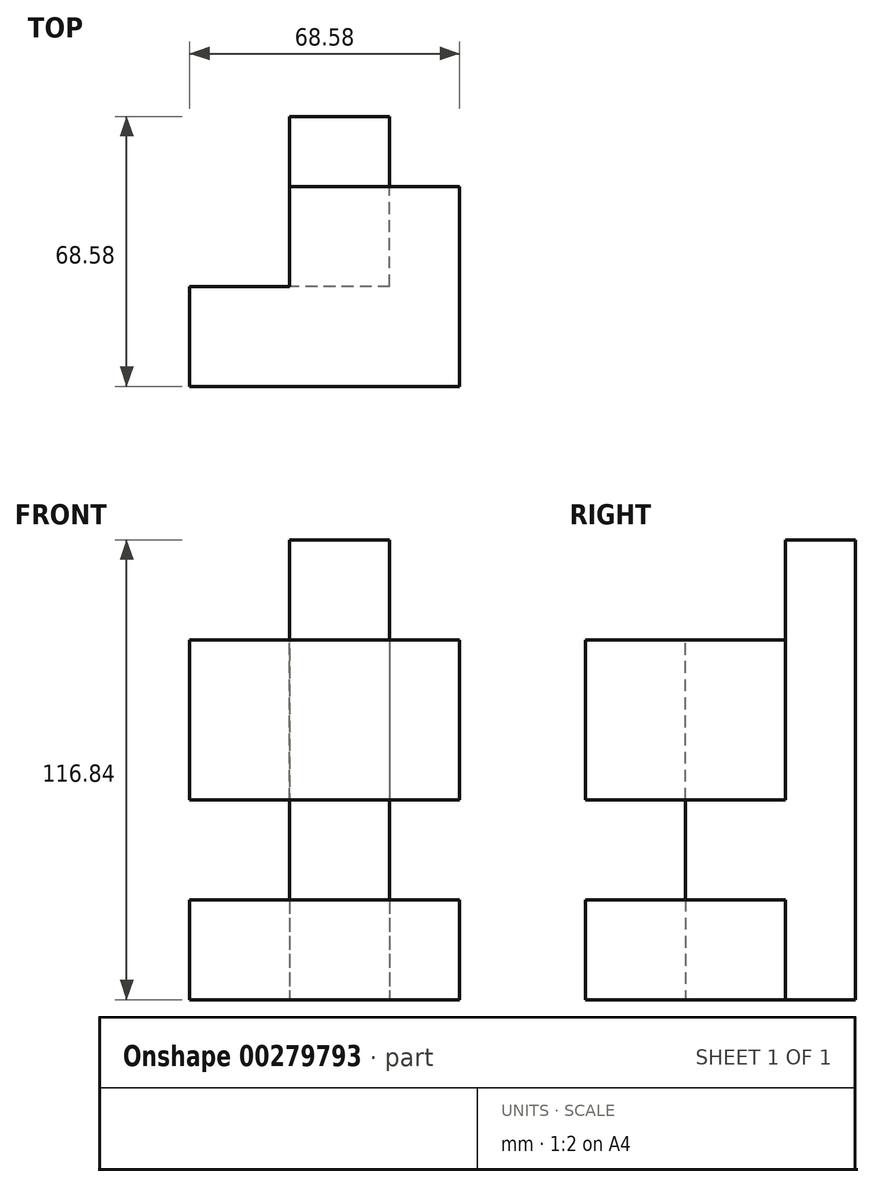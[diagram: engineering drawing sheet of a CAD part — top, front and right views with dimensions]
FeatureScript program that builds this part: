
annotation { "Feature Type Name" : "Feature", "Feature Type Description" : "" }
export const myFeature = defineFeature(function(context is Context, id is Id, definition is map)
    precondition{}
    {
        {
            var Q0;
            Q0=qCreatedBy(makeId("Front.planeOp"),FACE);
            var sketch = newSketch(context, id + "F0", { "sketchPlane" : qUnion([Q0])});
            skLineSegment(sketch, "E0.bottom", {"start": v(58.25, 55.3) * mm, "end": v(32.85, 55.3) * mm});
            skLineSegment(sketch, "E0.top", {"start": v(58.25, -61.53) * mm, "end": v(32.85, -61.53) * mm});
            skLineSegment(sketch, "E0.left", {"start": v(58.25, 55.3) * mm, "end": v(58.25, -61.53) * mm});
            skLineSegment(sketch, "E0.right", {"start": v(32.85, 55.3) * mm, "end": v(32.85, -61.53) * mm});
            skLineSegment(sketch, "E1", {"start": v(58.25, 29.9) * mm, "end": v(32.85, 29.9) * mm});
            skSolve(sketch);
        }
        {
            var Q0;
            {var subQ0=sQuery(id+"F0.wireOp",EDGE,"E0.bottom");Q0=makeQuery(id+"F0.imprint","IMPRINT",FACE,{"disambiguationData":[TD([[makeQuery(id+"F0.imprint","IMPRINT",EDGE,{"derivedFrom":subQ0}),1.0]])]});}
            extrude(context, id + "F1", {"entities" : qUnion([Q0]), "depth" : 17.78 * mm});
        }
        {
            var Q0;
            {var subQ0=sQuery(id+"F0.wireOp",EDGE,"E0.top");Q0=makeQuery(id+"F0.imprint","IMPRINT",FACE,{"disambiguationData":[TD([[makeQuery(id+"F0.imprint","IMPRINT",EDGE,{"derivedFrom":subQ0}),-1.0]])]});}
            extrude(context, id + "F2", {"entities" : qUnion([Q0]), "operationType" : NewBodyOperationType.ADD, "depth" : 68.58 * mm});
        }
        {
            var Q0;
            {var subQ0=sQuery(id+"F0.wireOp",EDGE,"E0.left");Q0=makeQuery(id+"F2.boolean.opBoolean","MERGE",FACE,{"derivedFrom":[makeQuery(id+"F1.opExtrude","SWEPT_FACE",FACE,{"disambiguationData":[OSD([subQ0])]}),makeQuery(id+"F2.opExtrude","SWEPT_FACE",FACE,{"disambiguationData":[OSD([subQ0])]})]});}
            var sketch = newSketch(context, id + "F3", { "sketchPlane" : qUnion([Q0])});
            skLineSegment(sketch, "E2", {"start": v(-17.78, 29.9) * mm, "end": v(-17.78, -61.53) * mm});
            skLineSegment(sketch, "E3", {"start": v(-68.58, -36.13) * mm, "end": v(-17.78, -36.13) * mm});
            skLineSegment(sketch, "E4", {"start": v(-68.58, -10.73) * mm, "end": v(-17.78, -10.73) * mm});
            skSolve(sketch);
        }
        {
            var Q0;
            {var subQ4=sQuery(id+"F3.wireOp",EDGE,"E3");Q0=makeQuery(id+"F3.imprint","IMPRINT",FACE,{"disambiguationData":[TD([[makeQuery(id+"F3.imprint","IMPRINT",EDGE,{"derivedFrom":subQ4}),-1.0]])]});}
            var Q1;
            {var subQ3=sQuery(id+"F3.wireOp",EDGE,"E4");Q1=makeQuery(id+"F3.imprint","IMPRINT",FACE,{"disambiguationData":[TD([[makeQuery(id+"F3.imprint","IMPRINT",EDGE,{"derivedFrom":subQ3}),1.0]])]});}
            extrude(context, id + "F4", {"entities" : qUnion([Q0, Q1]), "operationType" : NewBodyOperationType.ADD, "depth" : 17.78 * mm});
        }
        {
            var Q0;
            {var subQ0=sQuery(id+"F0.wireOp",EDGE,"E1");var subQ1=sQuery(id+"F0.wireOp",EDGE,"E0.left");var subQ2=makeQuery(id+"F2.opExtrude","CAP_EDGE",EDGE,{"disambiguationData":[OSD([subQ1])],"isStart":false});var subQ3=sQuery(id+"F0.wireOp",EDGE,"E0.top");Q0=makeQuery(id+"F4.boolean.opBoolean","MERGE",FACE,{"derivedFrom":[makeQuery(id+"F2.opExtrude","CAP_FACE",FACE,{"disambiguationData":[OSD([subQ3,subQ1,sQuery(id+"F0.wireOp",EDGE,"E0.right"),subQ0])],"isStart":false}),makeQuery(id+"F4.opExtrude","SWEPT_FACE",FACE,{"disambiguationData":[OSD([subQ1]),TDD([makeQuery(id+"F3.imprint","IMPRINT",EDGE,{"disambiguationData":[TD([[makeQuery(id+"F3.imprint","INTERSECT",VERTEX,{"derivedFrom":[subQ2,sQuery(id+"F3.wireOp",EDGE,"E3")]}),-1.0]])],"derivedFrom":subQ2})])]}),makeQuery(id+"F4.opExtrude","SWEPT_FACE",FACE,{"disambiguationData":[OSD([subQ1]),TDD([makeQuery(id+"F3.imprint","IMPRINT",EDGE,{"disambiguationData":[TD([[makeQuery(id+"F3.imprint","INTERSECT",VERTEX,{"derivedFrom":[subQ2,sQuery(id+"F3.wireOp",EDGE,"E4")]}),1.0]])],"derivedFrom":subQ2})])]})]});}
            var sketch = newSketch(context, id + "F5", { "sketchPlane" : qUnion([Q0])});
            skLineSegment(sketch, "E5", {"start": v(58.25, -10.73) * mm, "end": v(32.85, -10.73) * mm});
            skLineSegment(sketch, "E6", {"start": v(58.25, -36.13) * mm, "end": v(32.85, -36.13) * mm});
            skSolve(sketch);
        }
        {
            var Q0;
            {var subQ0=sQuery(id+"F5.wireOp",EDGE,"E5");Q0=makeQuery(id+"F5.imprint","IMPRINT",FACE,{"disambiguationData":[TD([[makeQuery(id+"F5.imprint","IMPRINT",EDGE,{"derivedFrom":subQ0}),1.0]])]});}
            extrude(context, id + "F6", {"entities" : qUnion([Q0]), "operationType" : NewBodyOperationType.REMOVE, "oppositeDirection" : true, "depth" : 25.4 * mm});
        }
        {
            var Q0;
            {var subQ0=sQuery(id+"F0.wireOp",EDGE,"E0.right");Q0=makeQuery(id+"F2.boolean.opBoolean","MERGE",FACE,{"derivedFrom":[makeQuery(id+"F1.opExtrude","SWEPT_FACE",FACE,{"disambiguationData":[OSD([subQ0])]}),makeQuery(id+"F2.opExtrude","SWEPT_FACE",FACE,{"disambiguationData":[OSD([subQ0])]})]});}
            var sketch = newSketch(context, id + "F7", { "sketchPlane" : qUnion([Q0])});
            skLineSegment(sketch, "E7", {"start": v(43.18, -36.13) * mm, "end": v(43.18, -61.53) * mm});
            skLineSegment(sketch, "E8", {"start": v(43.18, -10.73) * mm, "end": v(43.18, 29.9) * mm});
            skSolve(sketch);
        }
        {
            var Q0;
            {var subQ0=sQuery(id+"F7.wireOp",EDGE,"E7");Q0=makeQuery(id+"F7.imprint","IMPRINT",FACE,{"disambiguationData":[TD([[makeQuery(id+"F7.imprint","IMPRINT",EDGE,{"derivedFrom":subQ0}),1.0]])]});}
            var Q1;
            {var subQ0=sQuery(id+"F7.wireOp",EDGE,"E8");Q1=makeQuery(id+"F7.imprint","IMPRINT",FACE,{"disambiguationData":[TD([[makeQuery(id+"F7.imprint","IMPRINT",EDGE,{"derivedFrom":subQ0}),-1.0]])]});}
            extrude(context, id + "F8", {"entities" : qUnion([Q0, Q1]), "operationType" : NewBodyOperationType.ADD, "depth" : 25.4 * mm});
        }
    });
